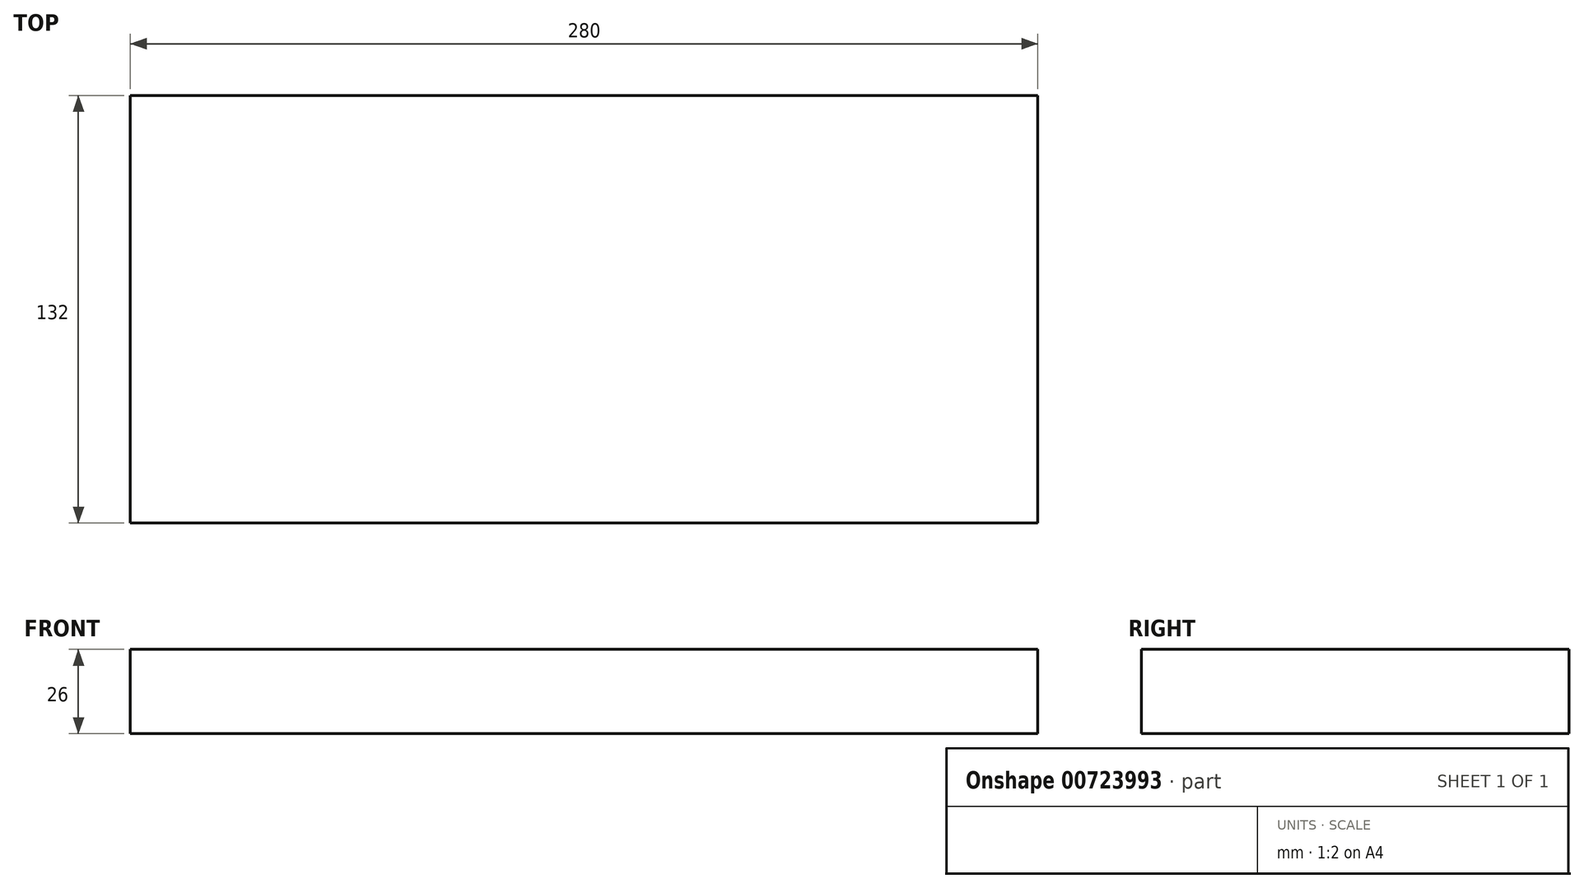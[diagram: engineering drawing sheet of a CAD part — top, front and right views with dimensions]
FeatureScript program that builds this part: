
annotation { "Feature Type Name" : "Feature", "Feature Type Description" : "" }
export const myFeature = defineFeature(function(context is Context, id is Id, definition is map)
    precondition{}
    {
        {
            var Q0;
            Q0=qCreatedBy(makeId("Top.planeOp"),FACE);
            var sketch = newSketch(context, id + "F0", { "sketchPlane" : qUnion([Q0])});
            skLineSegment(sketch, "E0.bottom", {"start": v(-140, 66) * mm, "end": v(140, 66) * mm});
            skLineSegment(sketch, "E0.top", {"start": v(-140, -66) * mm, "end": v(140, -66) * mm});
            skLineSegment(sketch, "E0.left", {"start": v(-140, 66) * mm, "end": v(-140, -66) * mm});
            skLineSegment(sketch, "E0.right", {"start": v(140, 66) * mm, "end": v(140, -66) * mm});
            skLineSegment(sketch, "E1", {"start": v(-140, 66) * mm, "end": v(140, -66) * mm, "construction": true});
            skLineSegment(sketch, "E2", {"start": v(140, 66) * mm, "end": v(-140, -66) * mm, "construction": true});
            skSolve(sketch);
        }
        {
            var Q0;
            Q0=qSketchRegion(id+"F0",true);
            extrude(context, id + "F1", {"entities" : qUnion([Q0]), "depth" : 26 * mm, "offsetDistance" : 25 * mm});
        }
    });
